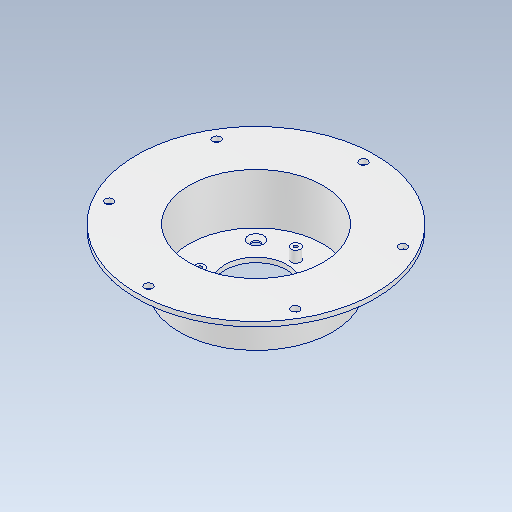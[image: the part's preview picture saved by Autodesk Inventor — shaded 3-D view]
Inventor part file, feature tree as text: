
AUTODESK INVENTOR PART (.ipt)
format: ipt  version: 2021 (Build 250183000, 183)  size: 205,824 bytes
history: native  units: in
note: dims shown in document units (in); Inventor stores cm internally (conversion verified against a paired STEP export)
features: sketch x5, hole x3, projected_geometry x3, revolve x1, fillet x1, extrude x1
ambient origin geometry x8: Origin, YZ Plane, XZ Plane, XY Plane, X Axis, Y Axis, Z Axis, Center Point
bodies: Solid1 (feature_tree)
feature tree (14):
  revolve  "Revolution1"  [1 undecoded]
  hole  "Hole1"  [1 undecoded]
  hole  "Hole2"  [1 undecoded]
  fillet  "Fillet1"  Radius=1.2205in
  extrude  "Extrusion1"  Depth=0.0787in
  hole  "Hole3"  [1 undecoded]
  sketch  "Sketch1"  dims[d0=0.0787in d1=0.0787in]
  sketch  "Sketch2"  dims[d4=1.9685in d7=0.5118in]
  sketch  "Sketch3"  dims[d10=90.0deg d11=0.7559in d14=1.2205in]
  sketch  "Sketch4"  dims[d15=1.2205in]
  sketch  "Sketch5"  dims[d16=0.1339in d17=0.1969in d18=0.248in d19=0.0787in d20=90.0deg d21=0.2559in d22=0.8108in d23=3.5433in d24=2.3622in d26=360.0deg d28=0.1339in d29=0.1969in d30=0.248in d31=0.0787in d32=90.0deg d33=0.2559in d34=0.8108in d35=1.2598in d36=0.1575in d37=0.8346in d38=0.1969in d39=0.1575in d45=0.187in d46=0.0in d47=0.0617in d48=0.1575in d49=0.248in d50=0.0787in d51=90.0deg d52=0.248in d53=0.8108in d54=0.6535in d55=0.1575in d56=0.9843in d57=0.4331in]
  projected_geometry  "Projected Loop1"
  projected_geometry  "Projected Loop4"
  projected_geometry  "Projected Loop5"
note: 4 required parameter values undecoded (feature->parameter linkage not recoverable at this tier; creation-order binding heuristic only, values carry confidence <= 0.55)